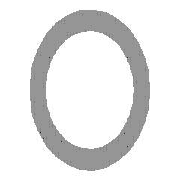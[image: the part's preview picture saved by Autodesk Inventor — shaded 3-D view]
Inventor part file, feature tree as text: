
AUTODESK INVENTOR PART (.ipt)
format: ipt  version: 2021 (Build 250183000, 183)  size: 408,576 bytes
history: native  units: mm (DEFAULTED — no unit token found)
features: other x7, plane x3, sketch x3, sweep x1, split x1
ambient origin geometry x8: Origin, YZ Plane, XZ Plane, XY Plane, X Axis, Y Axis, Z Axis, Center Point
bodies: Solid1 (feature_tree)
feature tree (15):
  parser-record x1  (decoder bookkeeping rows leaked as tree rows — omitted from the tree; the rows remain in map.json)
  other  "Driven Length"
  other  "Plano inicial"
  other  "Plano final"
  other  "Trayectoria de barrido"
  plane  "Plano de trabajo de orientación"
  sweep  "Cuerpo"
  plane  "Plano de trabajo8"
  split  "Dividir4"
  sketch  "Sketch3"  dims[d0=26.67mm d1=3.9116mm]
  plane  "Work Plane3"
  sketch  "Sketch4"  dims[d4=-0.0mm]
  sketch  "Boceto8"  dims[d5=1126.193571mm d6=90.0deg d7=1126.193571mm d8=0.0mm d9=0.0mm d22=0.0mm d23=90.0deg d24=0.0mm d25=90.0deg]
  other  "Sup4"
  other  "SuperficieSolevación4"
